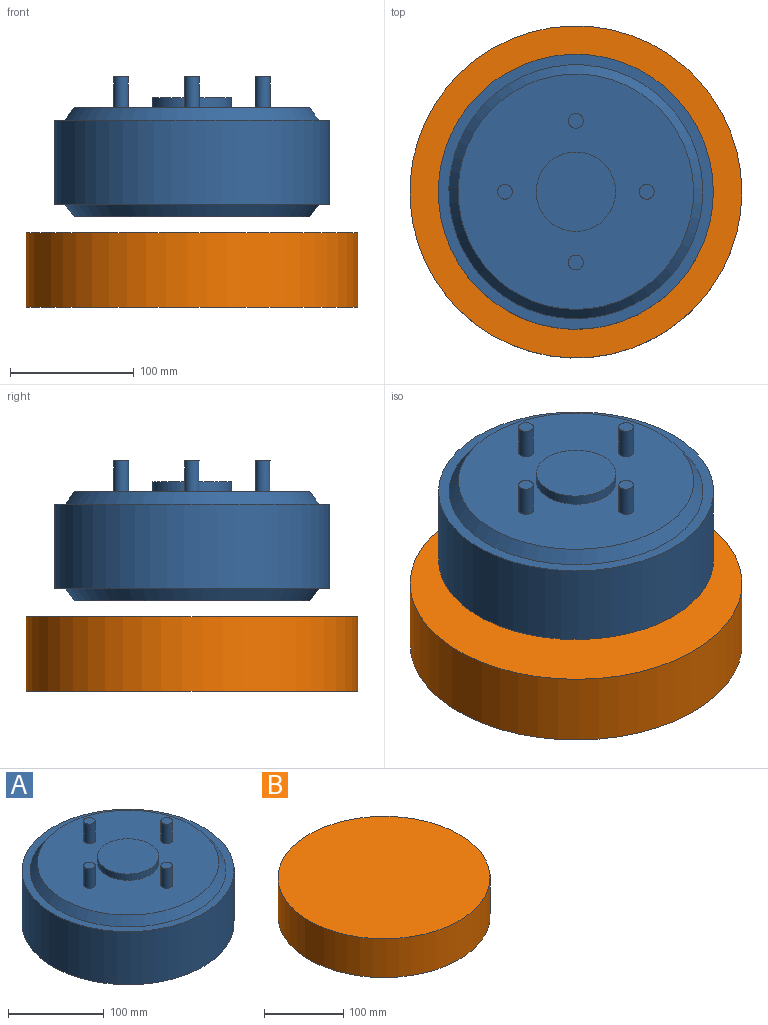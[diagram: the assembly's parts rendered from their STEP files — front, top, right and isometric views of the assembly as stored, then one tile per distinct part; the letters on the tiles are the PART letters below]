
ASSEMBLY  parts=2 mates=1
PART A: 17 faces, bbox 222x222x113 mm
  f0: cylinder r=111mm len=222mm, axis (0,0,-1), area 47425.5mm2, adj f1,f2
  f1: plane 222x222mm, normal (0,0,1), area 5701.2mm2, adj f0,f3
  f2: plane 222x222mm, normal (0,0,-1), area 5701.2mm2, adj f0,f7
  f3: cone r=102.5mm half-angle=36.9deg, axis (0,0,-1), area 7755.8mm2, adj f1,f4
  f4: plane 190x190mm, normal (0,0,1), area 24673.4mm2, adj f3,f5,f9,f11,f13,f15
  f5: cylinder r=32.05mm len=64.1mm, axis (0,0,1), area 1611mm2, adj f4,f6
  f6: plane 64.1x64.1mm, normal (0,0,1), area 3227.1mm2, adj f5
  f7: cone r=102.5mm half-angle=36.9deg, axis (0,0,1), area 7755.8mm2, adj f2,f8
  f8: plane 190x190mm, normal (0,0,-1), area 28352.9mm2, adj f7
  f9: cylinder r=6mm len=25mm, axis (0,0,-1), area 942.5mm2, adj f4,f10
  f10: plane 12x12mm, normal (0,0,1), area 113.1mm2, adj f9
  f11: cylinder r=6mm len=25mm, axis (0,0,-1), area 942.5mm2, adj f4,f12
  f12: plane 12x12mm, normal (0,0,1), area 113.1mm2, adj f11
  f13: cylinder r=6mm len=25mm, axis (0,0,-1), area 942.5mm2, adj f4,f14
  f14: plane 12x12mm, normal (0,0,1), area 113.1mm2, adj f13
  f15: cylinder r=6mm len=25mm, axis (0,0,-1), area 942.5mm2, adj f4,f16
  f16: plane 12x12mm, normal (0,0,1), area 113.1mm2, adj f15
PART B: 3 faces, bbox 268x268x59.9 mm
  f0: cylinder r=133.98mm len=267.97mm, axis (0,0,-1), area 50464mm2, adj f1,f2
  f1: plane 267.97x267.97mm, normal (0,0,1), area 56397.8mm2, adj f0
  f2: plane 267.97x267.97mm, normal (0,0,-1), area 56397.8mm2, adj f0
PLACE A t=(126.09,81.66,91.52)mm
PLACE B t=(126.09,81.66,8.55)mm
MATE cylindrical A.f3 <-> B.f0  axis (0,0,1) through (126.09,81.66,173.52)mm
